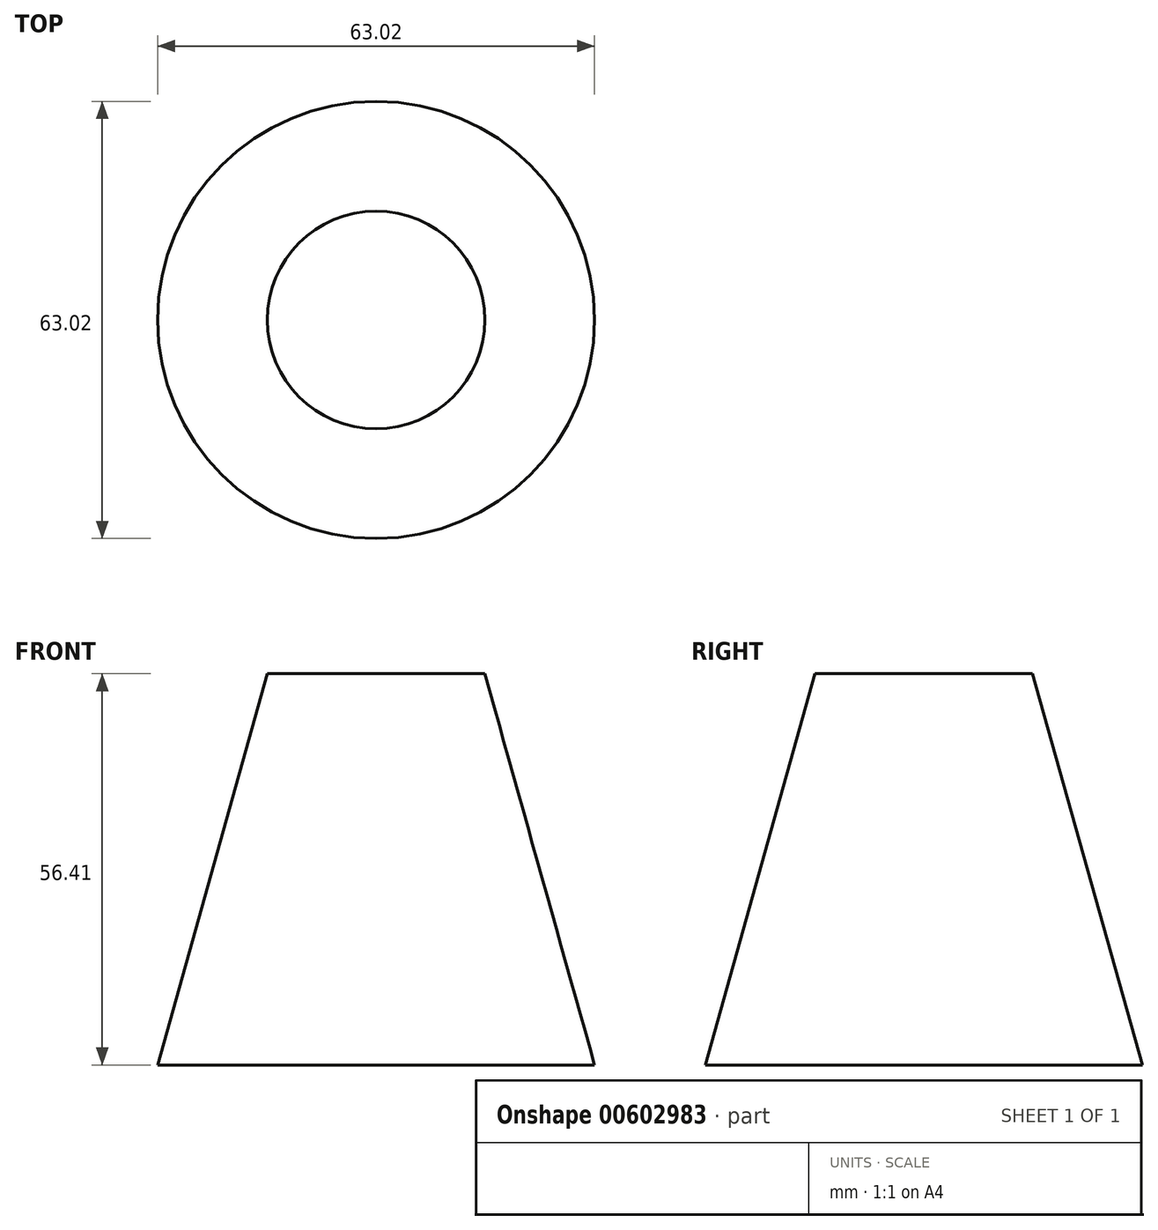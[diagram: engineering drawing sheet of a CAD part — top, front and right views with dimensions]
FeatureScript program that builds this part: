
annotation { "Feature Type Name" : "Feature", "Feature Type Description" : "" }
export const myFeature = defineFeature(function(context is Context, id is Id, definition is map)
    precondition{}
    {
        {
            var Q0;
            Q0=qCreatedBy(makeId("Front.planeOp"),FACE);
            var sketch = newSketch(context, id + "F0", { "sketchPlane" : qUnion([Q0])});
            skLineSegment(sketch, "E0", {"start": v(0, 32.38) * mm, "end": v(15.69, 32.38) * mm});
            skLineSegment(sketch, "E1", {"start": v(0, -24.03) * mm, "end": v(31.51, -24.03) * mm});
            skLineSegment(sketch, "E2", {"start": v(15.69, 32.38) * mm, "end": v(31.51, -24.03) * mm});
            skLineSegment(sketch, "E3", {"start": v(0, 32.38) * mm, "end": v(0, -24.03) * mm});
            skSolve(sketch);
        }
        {
            var Q0;
            Q0=makeQuery(id+"F0.imprint","IMPRINT",FACE,{"disambiguationData":[TD([[makeQuery(id+"F0.imprint","IMPRINT",EDGE,{"derivedFrom":sQuery(id+"F0.wireOp",EDGE,"E0")}),-1.0]])]});
            var Q1;
            Q1=sQuery(id+"F0.wireOp",EDGE,"E3");
            revolve(context, id + "F1", {"entities" : qUnion([Q0]), "axis" : qUnion([Q1]), "revolveType" : RevolveType.FULL});
        }
    });
